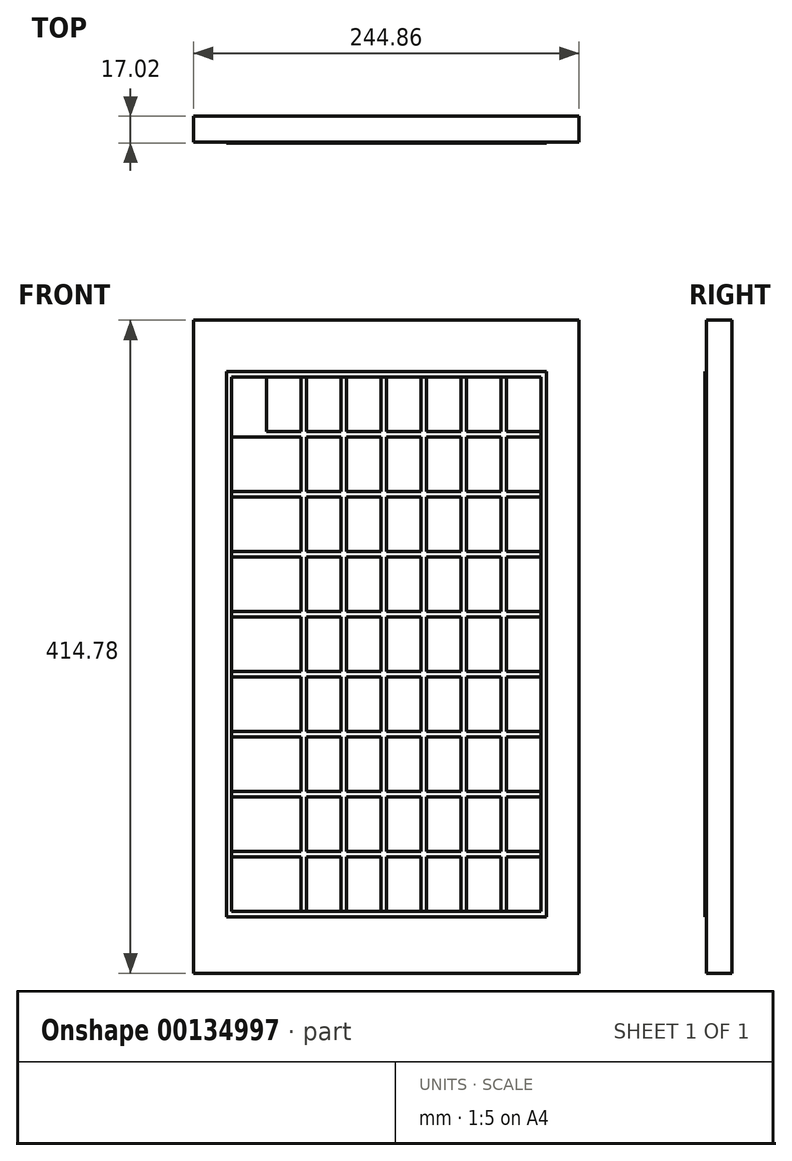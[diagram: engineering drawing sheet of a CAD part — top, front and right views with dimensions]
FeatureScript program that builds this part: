
annotation { "Feature Type Name" : "Feature", "Feature Type Description" : "" }
export const myFeature = defineFeature(function(context is Context, id is Id, definition is map)
    precondition{}
    {
        {
            var Q0;
            Q0=qCreatedBy(makeId("Front.planeOp"),FACE);
            var sketch = newSketch(context, id + "F0", { "sketchPlane" : qUnion([Q0])});
            skLineSegment(sketch, "E0.bottom", {"start": v(122.43, 207.4) * mm, "end": v(-122.43, 207.4) * mm});
            skLineSegment(sketch, "E0.top", {"start": v(122.43, -207.4) * mm, "end": v(-122.43, -207.4) * mm});
            skLineSegment(sketch, "E0.left", {"start": v(122.43, 207.4) * mm, "end": v(122.43, -207.4) * mm});
            skLineSegment(sketch, "E0.right", {"start": v(-122.43, 207.4) * mm, "end": v(-122.43, -207.4) * mm});
            skPoint(sketch, "E0.middle", {"position": v(0, 0) * mm});
            skSolve(sketch);
        }
        {
            var Q0;
            Q0=makeQuery(id+"F0.imprint","IMPRINT",FACE,{"disambiguationData":[TD([[makeQuery(id+"F0.imprint","IMPRINT",EDGE,{"derivedFrom":sQuery(id+"F0.wireOp",EDGE,"E0.bottom")}),1.0]])]});
            var sketch = newSketch(context, id + "F1", { "sketchPlane" : qUnion([Q0])});
            skLineSegment(sketch, "E1.bottom", {"start": v(98.22, 171.45) * mm, "end": v(-98.22, 171.45) * mm});
            skLineSegment(sketch, "E1.top", {"start": v(101.6, -171.45) * mm, "end": v(-101.6, -171.45) * mm});
            skLineSegment(sketch, "E1.left", {"start": v(101.6, 171.45) * mm, "end": v(101.6, -171.45) * mm});
            skLineSegment(sketch, "E1.right", {"start": v(-101.6, 171.45) * mm, "end": v(-101.6, -171.45) * mm});
            skPoint(sketch, "E1.middle", {"position": v(0, 0) * mm});
            skLineSegment(sketch, "E2.bottom", {"start": v(-98.22, 171.45) * mm, "end": v(-76.2, 171.45) * mm});
            skLineSegment(sketch, "E2.top", {"start": v(-98.22, 133.35) * mm, "end": v(-76.2, 133.35) * mm});
            skLineSegment(sketch, "E2.left", {"start": v(-101.6, 171.45) * mm, "end": v(-101.6, 133.35) * mm});
            skLineSegment(sketch, "E2.right", {"start": v(-76.2, 171.45) * mm, "end": v(-76.2, 133.35) * mm});
            skLineSegment(sketch, "E3.1.0.0", {"start": v(-50.8, 171.45) * mm, "end": v(-50.8, 133.35) * mm});
            skLineSegment(sketch, "E3.1.0.1", {"start": v(-76.2, 133.35) * mm, "end": v(-50.8, 133.35) * mm});
            skLineSegment(sketch, "E3.2.0.0", {"start": v(-25.4, 171.45) * mm, "end": v(-25.4, 133.35) * mm});
            skLineSegment(sketch, "E3.2.0.1", {"start": v(-50.8, 133.35) * mm, "end": v(-25.4, 133.35) * mm});
            skLineSegment(sketch, "E3.3.0.0", {"start": v(0, 171.45) * mm, "end": v(0, 133.35) * mm});
            skLineSegment(sketch, "E3.3.0.1", {"start": v(-25.4, 133.35) * mm, "end": v(0, 133.35) * mm});
            skLineSegment(sketch, "E3.4.0.0", {"start": v(25.4, 171.45) * mm, "end": v(25.4, 133.35) * mm});
            skLineSegment(sketch, "E3.4.0.1", {"start": v(0, 133.35) * mm, "end": v(25.4, 133.35) * mm});
            skLineSegment(sketch, "E3.5.0.0", {"start": v(50.8, 171.45) * mm, "end": v(50.8, 133.35) * mm});
            skLineSegment(sketch, "E3.5.0.1", {"start": v(25.4, 133.35) * mm, "end": v(50.8, 133.35) * mm});
            skLineSegment(sketch, "E3.6.0.0", {"start": v(76.2, 171.45) * mm, "end": v(76.2, 133.35) * mm});
            skLineSegment(sketch, "E3.6.0.1", {"start": v(50.8, 133.35) * mm, "end": v(76.2, 133.35) * mm});
            skLineSegment(sketch, "E3.7.0.0", {"start": v(101.6, 171.45) * mm, "end": v(101.6, 133.35) * mm});
            skLineSegment(sketch, "E3.7.0.1", {"start": v(76.2, 133.35) * mm, "end": v(98.22, 133.35) * mm});
            skLineSegment(sketch, "E3.direction1", {"start": v(-76.2, 133.35) * mm, "end": v(-50.8, 133.35) * mm, "construction": true});
            skLineSegment(sketch, "E4.0.1.0", {"start": v(-98.22, 95.25) * mm, "end": v(-76.2, 95.25) * mm});
            skLineSegment(sketch, "E4.0.1.1", {"start": v(-76.2, 133.35) * mm, "end": v(-76.2, 95.25) * mm});
            skLineSegment(sketch, "E4.0.2.0", {"start": v(-98.22, 57.15) * mm, "end": v(-76.2, 57.15) * mm});
            skLineSegment(sketch, "E4.0.2.1", {"start": v(-76.2, 95.25) * mm, "end": v(-76.2, 57.15) * mm});
            skLineSegment(sketch, "E4.0.3.0", {"start": v(-98.22, 19.05) * mm, "end": v(-76.2, 19.05) * mm});
            skLineSegment(sketch, "E4.0.3.1", {"start": v(-76.2, 57.15) * mm, "end": v(-76.2, 19.05) * mm});
            skLineSegment(sketch, "E4.0.4.0", {"start": v(-98.22, -19.05) * mm, "end": v(-76.2, -19.05) * mm});
            skLineSegment(sketch, "E4.0.4.1", {"start": v(-76.2, 19.05) * mm, "end": v(-76.2, -19.05) * mm});
            skLineSegment(sketch, "E4.0.5.0", {"start": v(-98.22, -57.15) * mm, "end": v(-76.2, -57.15) * mm});
            skLineSegment(sketch, "E4.0.5.1", {"start": v(-76.2, -19.05) * mm, "end": v(-76.2, -57.15) * mm});
            skLineSegment(sketch, "E4.0.6.0", {"start": v(-98.22, -95.25) * mm, "end": v(-76.2, -95.25) * mm});
            skLineSegment(sketch, "E4.0.6.1", {"start": v(-76.2, -57.15) * mm, "end": v(-76.2, -95.25) * mm});
            skLineSegment(sketch, "E4.0.7.0", {"start": v(-98.22, -133.35) * mm, "end": v(-76.2, -133.35) * mm});
            skLineSegment(sketch, "E4.0.7.1", {"start": v(-76.2, -95.25) * mm, "end": v(-76.2, -133.35) * mm});
            skLineSegment(sketch, "E4.0.8.0", {"start": v(-101.6, -171.45) * mm, "end": v(-76.2, -171.45) * mm});
            skLineSegment(sketch, "E4.0.8.1", {"start": v(-76.2, -133.35) * mm, "end": v(-76.2, -168.07) * mm});
            skLineSegment(sketch, "E4.1.1.0", {"start": v(-76.2, 95.25) * mm, "end": v(-50.8, 95.25) * mm});
            skLineSegment(sketch, "E4.1.1.1", {"start": v(-50.8, 133.35) * mm, "end": v(-50.8, 95.25) * mm});
            skLineSegment(sketch, "E4.1.2.0", {"start": v(-76.2, 57.15) * mm, "end": v(-50.8, 57.15) * mm});
            skLineSegment(sketch, "E4.1.2.1", {"start": v(-50.8, 95.25) * mm, "end": v(-50.8, 57.15) * mm});
            skLineSegment(sketch, "E4.1.3.0", {"start": v(-76.2, 19.05) * mm, "end": v(-50.8, 19.05) * mm});
            skLineSegment(sketch, "E4.1.3.1", {"start": v(-50.8, 57.15) * mm, "end": v(-50.8, 19.05) * mm});
            skLineSegment(sketch, "E4.1.4.0", {"start": v(-76.2, -19.05) * mm, "end": v(-50.8, -19.05) * mm});
            skLineSegment(sketch, "E4.1.4.1", {"start": v(-50.8, 19.05) * mm, "end": v(-50.8, -19.05) * mm});
            skLineSegment(sketch, "E4.1.5.0", {"start": v(-76.2, -57.15) * mm, "end": v(-50.8, -57.15) * mm});
            skLineSegment(sketch, "E4.1.5.1", {"start": v(-50.8, -19.05) * mm, "end": v(-50.8, -57.15) * mm});
            skLineSegment(sketch, "E4.1.6.0", {"start": v(-76.2, -95.25) * mm, "end": v(-50.8, -95.25) * mm});
            skLineSegment(sketch, "E4.1.6.1", {"start": v(-50.8, -57.15) * mm, "end": v(-50.8, -95.25) * mm});
            skLineSegment(sketch, "E4.1.7.0", {"start": v(-76.2, -133.35) * mm, "end": v(-50.8, -133.35) * mm});
            skLineSegment(sketch, "E4.1.7.1", {"start": v(-50.8, -95.25) * mm, "end": v(-50.8, -133.35) * mm});
            skLineSegment(sketch, "E4.1.8.0", {"start": v(-76.2, -171.45) * mm, "end": v(-50.8, -171.45) * mm});
            skLineSegment(sketch, "E4.1.8.1", {"start": v(-50.8, -133.35) * mm, "end": v(-50.8, -168.07) * mm});
            skLineSegment(sketch, "E4.2.1.0", {"start": v(-50.8, 95.25) * mm, "end": v(-25.4, 95.25) * mm});
            skLineSegment(sketch, "E4.2.1.1", {"start": v(-25.4, 133.35) * mm, "end": v(-25.4, 95.25) * mm});
            skLineSegment(sketch, "E4.2.2.0", {"start": v(-50.8, 57.15) * mm, "end": v(-25.4, 57.15) * mm});
            skLineSegment(sketch, "E4.2.2.1", {"start": v(-25.4, 95.25) * mm, "end": v(-25.4, 57.15) * mm});
            skLineSegment(sketch, "E4.2.3.0", {"start": v(-50.8, 19.05) * mm, "end": v(-25.4, 19.05) * mm});
            skLineSegment(sketch, "E4.2.3.1", {"start": v(-25.4, 57.15) * mm, "end": v(-25.4, 19.05) * mm});
            skLineSegment(sketch, "E4.2.4.0", {"start": v(-50.8, -19.05) * mm, "end": v(-25.4, -19.05) * mm});
            skLineSegment(sketch, "E4.2.4.1", {"start": v(-25.4, 19.05) * mm, "end": v(-25.4, -19.05) * mm});
            skLineSegment(sketch, "E4.2.5.0", {"start": v(-50.8, -57.15) * mm, "end": v(-25.4, -57.15) * mm});
            skLineSegment(sketch, "E4.2.5.1", {"start": v(-25.4, -19.05) * mm, "end": v(-25.4, -57.15) * mm});
            skLineSegment(sketch, "E4.2.6.0", {"start": v(-50.8, -95.25) * mm, "end": v(-25.4, -95.25) * mm});
            skLineSegment(sketch, "E4.2.6.1", {"start": v(-25.4, -57.15) * mm, "end": v(-25.4, -95.25) * mm});
            skLineSegment(sketch, "E4.2.7.0", {"start": v(-50.8, -133.35) * mm, "end": v(-25.4, -133.35) * mm});
            skLineSegment(sketch, "E4.2.7.1", {"start": v(-25.4, -95.25) * mm, "end": v(-25.4, -133.35) * mm});
            skLineSegment(sketch, "E4.2.8.0", {"start": v(-50.8, -171.45) * mm, "end": v(-25.4, -171.45) * mm});
            skLineSegment(sketch, "E4.2.8.1", {"start": v(-25.4, -133.35) * mm, "end": v(-25.4, -168.07) * mm});
            skLineSegment(sketch, "E4.3.1.0", {"start": v(-25.4, 95.25) * mm, "end": v(0, 95.25) * mm});
            skLineSegment(sketch, "E4.3.1.1", {"start": v(0, 133.35) * mm, "end": v(0, 95.25) * mm});
            skLineSegment(sketch, "E4.3.2.0", {"start": v(-25.4, 57.15) * mm, "end": v(0, 57.15) * mm});
            skLineSegment(sketch, "E4.3.2.1", {"start": v(0, 95.25) * mm, "end": v(0, 57.15) * mm});
            skLineSegment(sketch, "E4.3.3.0", {"start": v(-25.4, 19.05) * mm, "end": v(0, 19.05) * mm});
            skLineSegment(sketch, "E4.3.3.1", {"start": v(0, 57.15) * mm, "end": v(0, 19.05) * mm});
            skLineSegment(sketch, "E4.3.4.0", {"start": v(-25.4, -19.05) * mm, "end": v(0, -19.05) * mm});
            skLineSegment(sketch, "E4.3.4.1", {"start": v(0, 19.05) * mm, "end": v(0, -19.05) * mm});
            skLineSegment(sketch, "E4.3.5.0", {"start": v(-25.4, -57.15) * mm, "end": v(0, -57.15) * mm});
            skLineSegment(sketch, "E4.3.5.1", {"start": v(0, -19.05) * mm, "end": v(0, -57.15) * mm});
            skLineSegment(sketch, "E4.3.6.0", {"start": v(-25.4, -95.25) * mm, "end": v(0, -95.25) * mm});
            skLineSegment(sketch, "E4.3.6.1", {"start": v(0, -57.15) * mm, "end": v(0, -95.25) * mm});
            skLineSegment(sketch, "E4.3.7.0", {"start": v(-25.4, -133.35) * mm, "end": v(0, -133.35) * mm});
            skLineSegment(sketch, "E4.3.7.1", {"start": v(0, -95.25) * mm, "end": v(0, -133.35) * mm});
            skLineSegment(sketch, "E4.3.8.0", {"start": v(-25.4, -171.45) * mm, "end": v(0, -171.45) * mm});
            skLineSegment(sketch, "E4.3.8.1", {"start": v(0, -133.35) * mm, "end": v(0, -168.07) * mm});
            skLineSegment(sketch, "E4.4.1.0", {"start": v(0, 95.25) * mm, "end": v(25.4, 95.25) * mm});
            skLineSegment(sketch, "E4.4.1.1", {"start": v(25.4, 133.35) * mm, "end": v(25.4, 95.25) * mm});
            skLineSegment(sketch, "E4.4.2.0", {"start": v(0, 57.15) * mm, "end": v(25.4, 57.15) * mm});
            skLineSegment(sketch, "E4.4.2.1", {"start": v(25.4, 95.25) * mm, "end": v(25.4, 57.15) * mm});
            skLineSegment(sketch, "E4.4.3.0", {"start": v(0, 19.05) * mm, "end": v(25.4, 19.05) * mm});
            skLineSegment(sketch, "E4.4.3.1", {"start": v(25.4, 57.15) * mm, "end": v(25.4, 19.05) * mm});
            skLineSegment(sketch, "E4.4.4.0", {"start": v(0, -19.05) * mm, "end": v(25.4, -19.05) * mm});
            skLineSegment(sketch, "E4.4.4.1", {"start": v(25.4, 19.05) * mm, "end": v(25.4, -19.05) * mm});
            skLineSegment(sketch, "E4.4.5.0", {"start": v(0, -57.15) * mm, "end": v(25.4, -57.15) * mm});
            skLineSegment(sketch, "E4.4.5.1", {"start": v(25.4, -19.05) * mm, "end": v(25.4, -57.15) * mm});
            skLineSegment(sketch, "E4.4.6.0", {"start": v(0, -95.25) * mm, "end": v(25.4, -95.25) * mm});
            skLineSegment(sketch, "E4.4.6.1", {"start": v(25.4, -57.15) * mm, "end": v(25.4, -95.25) * mm});
            skLineSegment(sketch, "E4.4.7.0", {"start": v(0, -133.35) * mm, "end": v(25.4, -133.35) * mm});
            skLineSegment(sketch, "E4.4.7.1", {"start": v(25.4, -95.25) * mm, "end": v(25.4, -133.35) * mm});
            skLineSegment(sketch, "E4.4.8.0", {"start": v(0, -171.45) * mm, "end": v(25.4, -171.45) * mm});
            skLineSegment(sketch, "E4.4.8.1", {"start": v(25.4, -133.35) * mm, "end": v(25.4, -168.07) * mm});
            skLineSegment(sketch, "E4.5.1.0", {"start": v(25.4, 95.25) * mm, "end": v(50.8, 95.25) * mm});
            skLineSegment(sketch, "E4.5.1.1", {"start": v(50.8, 133.35) * mm, "end": v(50.8, 95.25) * mm});
            skLineSegment(sketch, "E4.5.2.0", {"start": v(25.4, 57.15) * mm, "end": v(50.8, 57.15) * mm});
            skLineSegment(sketch, "E4.5.2.1", {"start": v(50.8, 95.25) * mm, "end": v(50.8, 57.15) * mm});
            skLineSegment(sketch, "E4.5.3.0", {"start": v(25.4, 19.05) * mm, "end": v(50.8, 19.05) * mm});
            skLineSegment(sketch, "E4.5.3.1", {"start": v(50.8, 57.15) * mm, "end": v(50.8, 19.05) * mm});
            skLineSegment(sketch, "E4.5.4.0", {"start": v(25.4, -19.05) * mm, "end": v(50.8, -19.05) * mm});
            skLineSegment(sketch, "E4.5.4.1", {"start": v(50.8, 19.05) * mm, "end": v(50.8, -19.05) * mm});
            skLineSegment(sketch, "E4.5.5.0", {"start": v(25.4, -57.15) * mm, "end": v(50.8, -57.15) * mm});
            skLineSegment(sketch, "E4.5.5.1", {"start": v(50.8, -19.05) * mm, "end": v(50.8, -57.15) * mm});
            skLineSegment(sketch, "E4.5.6.0", {"start": v(25.4, -95.25) * mm, "end": v(50.8, -95.25) * mm});
            skLineSegment(sketch, "E4.5.6.1", {"start": v(50.8, -57.15) * mm, "end": v(50.8, -95.25) * mm});
            skLineSegment(sketch, "E4.5.7.0", {"start": v(25.4, -133.35) * mm, "end": v(50.8, -133.35) * mm});
            skLineSegment(sketch, "E4.5.7.1", {"start": v(50.8, -95.25) * mm, "end": v(50.8, -133.35) * mm});
            skLineSegment(sketch, "E4.5.8.0", {"start": v(25.4, -171.45) * mm, "end": v(50.8, -171.45) * mm});
            skLineSegment(sketch, "E4.5.8.1", {"start": v(50.8, -133.35) * mm, "end": v(50.8, -168.07) * mm});
            skLineSegment(sketch, "E4.6.1.0", {"start": v(50.8, 95.25) * mm, "end": v(76.2, 95.25) * mm});
            skLineSegment(sketch, "E4.6.1.1", {"start": v(76.2, 133.35) * mm, "end": v(76.2, 95.25) * mm});
            skLineSegment(sketch, "E4.6.2.0", {"start": v(50.8, 57.15) * mm, "end": v(76.2, 57.15) * mm});
            skLineSegment(sketch, "E4.6.2.1", {"start": v(76.2, 95.25) * mm, "end": v(76.2, 57.15) * mm});
            skLineSegment(sketch, "E4.6.3.0", {"start": v(50.8, 19.05) * mm, "end": v(76.2, 19.05) * mm});
            skLineSegment(sketch, "E4.6.3.1", {"start": v(76.2, 57.15) * mm, "end": v(76.2, 19.05) * mm});
            skLineSegment(sketch, "E4.6.4.0", {"start": v(50.8, -19.05) * mm, "end": v(76.2, -19.05) * mm});
            skLineSegment(sketch, "E4.6.4.1", {"start": v(76.2, 19.05) * mm, "end": v(76.2, -19.05) * mm});
            skLineSegment(sketch, "E4.6.5.0", {"start": v(50.8, -57.15) * mm, "end": v(76.2, -57.15) * mm});
            skLineSegment(sketch, "E4.6.5.1", {"start": v(76.2, -19.05) * mm, "end": v(76.2, -57.15) * mm});
            skLineSegment(sketch, "E4.6.6.0", {"start": v(50.8, -95.25) * mm, "end": v(76.2, -95.25) * mm});
            skLineSegment(sketch, "E4.6.6.1", {"start": v(76.2, -57.15) * mm, "end": v(76.2, -95.25) * mm});
            skLineSegment(sketch, "E4.6.7.0", {"start": v(50.8, -133.35) * mm, "end": v(76.2, -133.35) * mm});
            skLineSegment(sketch, "E4.6.7.1", {"start": v(76.2, -95.25) * mm, "end": v(76.2, -133.35) * mm});
            skLineSegment(sketch, "E4.6.8.0", {"start": v(50.8, -171.45) * mm, "end": v(76.2, -171.45) * mm});
            skLineSegment(sketch, "E4.6.8.1", {"start": v(76.2, -133.35) * mm, "end": v(76.2, -168.07) * mm});
            skLineSegment(sketch, "E4.7.1.0", {"start": v(76.2, 95.25) * mm, "end": v(98.22, 95.25) * mm});
            skLineSegment(sketch, "E4.7.1.1", {"start": v(101.6, 133.35) * mm, "end": v(101.6, 95.25) * mm});
            skLineSegment(sketch, "E4.7.2.0", {"start": v(76.2, 57.15) * mm, "end": v(98.22, 57.15) * mm});
            skLineSegment(sketch, "E4.7.2.1", {"start": v(101.6, 95.25) * mm, "end": v(101.6, 57.15) * mm});
            skLineSegment(sketch, "E4.7.3.0", {"start": v(76.2, 19.05) * mm, "end": v(98.22, 19.05) * mm});
            skLineSegment(sketch, "E4.7.3.1", {"start": v(101.6, 57.15) * mm, "end": v(101.6, 19.05) * mm});
            skLineSegment(sketch, "E4.7.4.0", {"start": v(76.2, -19.05) * mm, "end": v(98.22, -19.05) * mm});
            skLineSegment(sketch, "E4.7.4.1", {"start": v(101.6, 19.05) * mm, "end": v(101.6, -19.05) * mm});
            skLineSegment(sketch, "E4.7.5.0", {"start": v(76.2, -57.15) * mm, "end": v(98.22, -57.15) * mm});
            skLineSegment(sketch, "E4.7.5.1", {"start": v(101.6, -19.05) * mm, "end": v(101.6, -57.15) * mm});
            skLineSegment(sketch, "E4.7.6.0", {"start": v(76.2, -95.25) * mm, "end": v(98.22, -95.25) * mm});
            skLineSegment(sketch, "E4.7.6.1", {"start": v(101.6, -57.15) * mm, "end": v(101.6, -95.25) * mm});
            skLineSegment(sketch, "E4.7.7.0", {"start": v(76.2, -133.35) * mm, "end": v(98.22, -133.35) * mm});
            skLineSegment(sketch, "E4.7.7.1", {"start": v(101.6, -95.25) * mm, "end": v(101.6, -133.35) * mm});
            skLineSegment(sketch, "E4.7.8.0", {"start": v(76.2, -171.45) * mm, "end": v(101.6, -171.45) * mm});
            skLineSegment(sketch, "E4.7.8.1", {"start": v(101.6, -133.35) * mm, "end": v(101.6, -171.45) * mm});
            skLineSegment(sketch, "E4.direction1", {"start": v(-98.22, 133.35) * mm, "end": v(-76.2, 133.35) * mm, "construction": true});
            skLineSegment(sketch, "E4.direction2", {"start": v(-101.6, 133.35) * mm, "end": v(-101.6, 95.25) * mm, "construction": true});
            skLineSegment(sketch, "E5.0", {"start": v(98.22, 171.45) * mm, "end": v(98.22, -168.07) * mm});
            skLineSegment(sketch, "E6.0", {"start": v(-98.22, 171.45) * mm, "end": v(-98.22, -168.07) * mm});
            skLineSegment(sketch, "E7.1.0.0", {"start": v(72.82, 171.45) * mm, "end": v(72.82, -168.07) * mm});
            skLineSegment(sketch, "E7.2.0.0", {"start": v(47.42, 171.45) * mm, "end": v(47.42, -168.07) * mm});
            skLineSegment(sketch, "E7.3.0.0", {"start": v(22.02, 171.45) * mm, "end": v(22.02, -168.07) * mm});
            skLineSegment(sketch, "E7.4.0.0", {"start": v(-3.38, 171.45) * mm, "end": v(-3.38, -168.07) * mm});
            skLineSegment(sketch, "E7.5.0.0", {"start": v(-28.78, 171.45) * mm, "end": v(-28.78, -168.07) * mm});
            skLineSegment(sketch, "E7.6.0.0", {"start": v(-54.18, 171.45) * mm, "end": v(-54.18, -168.07) * mm});
            skLineSegment(sketch, "E7.7.0.0", {"start": v(-79.58, 171.45) * mm, "end": v(-79.58, -168.07) * mm});
            skLineSegment(sketch, "E7.direction1", {"start": v(98.22, -171.45) * mm, "end": v(72.82, -171.45) * mm, "construction": true});
            skLineSegment(sketch, "E8.0", {"start": v(98.22, -168.07) * mm, "end": v(-98.22, -168.07) * mm});
            skLineSegment(sketch, "E9.0.1.0", {"start": v(98.22, -129.97) * mm, "end": v(-98.22, -129.97) * mm});
            skLineSegment(sketch, "E9.0.2.0", {"start": v(98.22, -91.87) * mm, "end": v(-98.22, -91.87) * mm});
            skLineSegment(sketch, "E9.0.3.0", {"start": v(98.22, -53.77) * mm, "end": v(-98.22, -53.77) * mm});
            skLineSegment(sketch, "E9.0.4.0", {"start": v(98.22, -15.67) * mm, "end": v(-98.22, -15.67) * mm});
            skLineSegment(sketch, "E9.0.5.0", {"start": v(98.22, 22.43) * mm, "end": v(-98.22, 22.43) * mm});
            skLineSegment(sketch, "E9.0.6.0", {"start": v(98.22, 60.53) * mm, "end": v(-98.22, 60.53) * mm});
            skLineSegment(sketch, "E9.0.7.0", {"start": v(98.22, 98.63) * mm, "end": v(-98.22, 98.63) * mm});
            skLineSegment(sketch, "E9.0.8.0", {"start": v(98.22, 136.73) * mm, "end": v(-98.22, 136.73) * mm});
            skLineSegment(sketch, "E9.1.0.0", {"start": v(98.22, -168.07) * mm, "end": v(-76.2, -168.07) * mm});
            skLineSegment(sketch, "E9.1.1.0", {"start": v(98.22, -129.97) * mm, "end": v(-76.2, -129.97) * mm});
            skLineSegment(sketch, "E9.1.2.0", {"start": v(98.22, -91.87) * mm, "end": v(-76.2, -91.87) * mm});
            skLineSegment(sketch, "E9.1.3.0", {"start": v(98.22, -53.77) * mm, "end": v(-76.2, -53.77) * mm});
            skLineSegment(sketch, "E9.1.4.0", {"start": v(98.22, -15.67) * mm, "end": v(-76.2, -15.67) * mm});
            skLineSegment(sketch, "E9.1.5.0", {"start": v(98.22, 22.43) * mm, "end": v(-76.2, 22.43) * mm});
            skLineSegment(sketch, "E9.1.6.0", {"start": v(98.22, 60.53) * mm, "end": v(-76.2, 60.53) * mm});
            skLineSegment(sketch, "E9.1.7.0", {"start": v(98.22, 98.63) * mm, "end": v(-76.2, 98.63) * mm});
            skLineSegment(sketch, "E9.1.8.0", {"start": v(98.22, 136.73) * mm, "end": v(-76.2, 136.73) * mm});
            skLineSegment(sketch, "E9.2.0.0", {"start": v(98.22, -168.07) * mm, "end": v(-50.8, -168.07) * mm});
            skLineSegment(sketch, "E9.2.1.0", {"start": v(98.22, -129.97) * mm, "end": v(-50.8, -129.97) * mm});
            skLineSegment(sketch, "E9.2.2.0", {"start": v(98.22, -91.87) * mm, "end": v(-50.8, -91.87) * mm});
            skLineSegment(sketch, "E9.2.3.0", {"start": v(98.22, -53.77) * mm, "end": v(-50.8, -53.77) * mm});
            skLineSegment(sketch, "E9.2.4.0", {"start": v(98.22, -15.67) * mm, "end": v(-50.8, -15.67) * mm});
            skLineSegment(sketch, "E9.2.5.0", {"start": v(98.22, 22.43) * mm, "end": v(-50.8, 22.43) * mm});
            skLineSegment(sketch, "E9.2.6.0", {"start": v(98.22, 60.53) * mm, "end": v(-50.8, 60.53) * mm});
            skLineSegment(sketch, "E9.2.7.0", {"start": v(98.22, 98.63) * mm, "end": v(-50.8, 98.63) * mm});
            skLineSegment(sketch, "E9.2.8.0", {"start": v(98.22, 136.73) * mm, "end": v(-50.8, 136.73) * mm});
            skLineSegment(sketch, "E9.direction1", {"start": v(-98.22, -168.07) * mm, "end": v(-76.2, -168.07) * mm, "construction": true});
            skLineSegment(sketch, "E9.direction2", {"start": v(-101.6, -168.07) * mm, "end": v(-101.6, -129.97) * mm, "construction": true});
            skPoint(sketch, "E10.orphan", {"position": v(152.4, 136.73) * mm});
            skPoint(sketch, "E11.orphan", {"position": v(127, 136.73) * mm});
            skPoint(sketch, "E12.orphan", {"position": v(152.4, 98.63) * mm});
            skPoint(sketch, "E13.orphan", {"position": v(152.4, 60.53) * mm});
            skPoint(sketch, "E14.orphan", {"position": v(127, 98.63) * mm});
            skPoint(sketch, "E15.orphan", {"position": v(127, 60.53) * mm});
            skPoint(sketch, "E16.orphan", {"position": v(152.4, 22.43) * mm});
            skPoint(sketch, "E17.orphan", {"position": v(127, 22.43) * mm});
            skPoint(sketch, "E18.orphan", {"position": v(152.4, -15.67) * mm});
            skPoint(sketch, "E19.orphan", {"position": v(152.4, -53.77) * mm});
            skPoint(sketch, "E20.orphan", {"position": v(127, -15.67) * mm});
            skPoint(sketch, "E21.orphan", {"position": v(127, -53.77) * mm});
            skPoint(sketch, "E22.orphan", {"position": v(152.4, -91.87) * mm});
            skPoint(sketch, "E23.orphan", {"position": v(152.4, -129.97) * mm});
            skPoint(sketch, "E24.orphan", {"position": v(152.4, -168.07) * mm});
            skPoint(sketch, "E25.orphan", {"position": v(127, -168.07) * mm});
            skPoint(sketch, "E26.orphan", {"position": v(127, -129.97) * mm});
            skPoint(sketch, "E27.orphan", {"position": v(127, -91.87) * mm});
            skLineSegment(sketch, "E28", {"start": v(-101.6, 171.45) * mm, "end": v(-101.6, 174.83) * mm});
            skLineSegment(sketch, "E29", {"start": v(-101.6, 174.83) * mm, "end": v(98.22, 174.83) * mm});
            skLineSegment(sketch, "E30", {"start": v(98.22, 174.83) * mm, "end": v(101.6, 174.83) * mm});
            skLineSegment(sketch, "E31", {"start": v(101.6, 174.83) * mm, "end": v(101.6, 171.45) * mm});
            skPoint(sketch, "E32.orphan", {"position": v(-101.6, 136.73) * mm});
            skPoint(sketch, "E33.orphan", {"position": v(-101.6, 98.63) * mm});
            skPoint(sketch, "E34.orphan", {"position": v(-101.6, 60.53) * mm});
            skPoint(sketch, "E35.orphan", {"position": v(-101.6, 57.15) * mm});
            skPoint(sketch, "E36.orphan", {"position": v(-101.6, 22.43) * mm});
            skPoint(sketch, "E37.orphan", {"position": v(-101.6, 19.05) * mm});
            skPoint(sketch, "E38.orphan", {"position": v(-101.6, -15.67) * mm});
            skPoint(sketch, "E39.orphan", {"position": v(-101.6, -19.05) * mm});
            skPoint(sketch, "E40.orphan", {"position": v(-101.6, -53.77) * mm});
            skPoint(sketch, "E41.orphan", {"position": v(-101.6, -57.15) * mm});
            skPoint(sketch, "E42.orphan", {"position": v(-101.6, -91.87) * mm});
            skPoint(sketch, "E43.orphan", {"position": v(-101.6, -95.25) * mm});
            skPoint(sketch, "E44.orphan", {"position": v(-101.6, -133.35) * mm});
            skPoint(sketch, "E45.orphan", {"position": v(-98.22, -171.45) * mm});
            skPoint(sketch, "E46.orphan", {"position": v(-79.58, -171.45) * mm});
            skPoint(sketch, "E47.orphan", {"position": v(-54.18, -171.45) * mm});
            skPoint(sketch, "E48.orphan", {"position": v(-28.78, -171.45) * mm});
            skPoint(sketch, "E49.orphan", {"position": v(-3.38, -171.45) * mm});
            skPoint(sketch, "E50.orphan", {"position": v(22.02, -171.45) * mm});
            skPoint(sketch, "E51.orphan", {"position": v(47.42, -171.45) * mm});
            skPoint(sketch, "E52.orphan", {"position": v(101.6, -168.07) * mm});
            skPoint(sketch, "E53.orphan", {"position": v(101.6, -129.97) * mm});
            skPoint(sketch, "E54.orphan", {"position": v(101.6, -91.87) * mm});
            skPoint(sketch, "E55.orphan", {"position": v(101.6, -53.77) * mm});
            skPoint(sketch, "E56.orphan", {"position": v(101.6, -15.67) * mm});
            skPoint(sketch, "E57.orphan", {"position": v(101.6, 22.43) * mm});
            skPoint(sketch, "E58.orphan", {"position": v(101.6, 60.53) * mm});
            skPoint(sketch, "E59.orphan", {"position": v(101.6, 98.63) * mm});
            skPoint(sketch, "E60.orphan", {"position": v(101.6, 136.73) * mm});
            skSolve(sketch);
        }
        {
            var Q0;
            Q0=makeQuery(id+"F0.imprint","IMPRINT",FACE,{"disambiguationData":[TD([[makeQuery(id+"F0.imprint","IMPRINT",EDGE,{"derivedFrom":sQuery(id+"F0.wireOp",EDGE,"E0.bottom")}),1.0]])]});
            extrude(context, id + "F2", {"entities" : qUnion([Q0]), "depth" : 16.26 * mm});
        }
        {
            var Q0;
            {var subQ0=sQuery(id+"F1.wireOp",EDGE,"E3.6.0.0");var subQ1=sQuery(id+"F1.wireOp",EDGE,"E1.bottom");var subQ2=makeQuery(id+"F1.imprint","INTERSECT",VERTEX,{"derivedFrom":[subQ1,subQ0]});Q0=makeQuery(id+"F1.imprint","IMPRINT",FACE,{"disambiguationData":[TD([[makeQuery(id+"F1.imprint","IMPRINT",EDGE,{"disambiguationData":[TD([[subQ2,1.0]])],"derivedFrom":subQ1}),1.0]])]});}
            var Q1;
            {var subQ0=sQuery(id+"F1.wireOp",EDGE,"E3.7.0.1");var subQ5=sQuery(id+"F1.wireOp",EDGE,"E5.0");var subQ6=makeQuery(id+"F1.imprint","INTERSECT",VERTEX,{"derivedFrom":[subQ0,subQ5]});Q1=makeQuery(id+"F1.imprint","IMPRINT",FACE,{"disambiguationData":[TD([[makeQuery(id+"F1.imprint","IMPRINT",EDGE,{"disambiguationData":[TD([[subQ6,-1.0]])],"derivedFrom":subQ5}),-1.0]])]});}
            var Q2;
            {var subQ0=sQuery(id+"F1.wireOp",EDGE,"E4.7.1.0");var subQ5=sQuery(id+"F1.wireOp",EDGE,"E5.0");var subQ6=makeQuery(id+"F1.imprint","INTERSECT",VERTEX,{"derivedFrom":[subQ0,subQ5]});Q2=makeQuery(id+"F1.imprint","IMPRINT",FACE,{"disambiguationData":[TD([[makeQuery(id+"F1.imprint","IMPRINT",EDGE,{"disambiguationData":[TD([[subQ6,-1.0]])],"derivedFrom":subQ5}),-1.0]])]});}
            var Q3;
            {var subQ0=sQuery(id+"F1.wireOp",EDGE,"E4.7.2.0");var subQ5=sQuery(id+"F1.wireOp",EDGE,"E5.0");var subQ6=makeQuery(id+"F1.imprint","INTERSECT",VERTEX,{"derivedFrom":[subQ0,subQ5]});Q3=makeQuery(id+"F1.imprint","IMPRINT",FACE,{"disambiguationData":[TD([[makeQuery(id+"F1.imprint","IMPRINT",EDGE,{"disambiguationData":[TD([[subQ6,-1.0]])],"derivedFrom":subQ5}),-1.0]])]});}
            var Q4;
            {var subQ0=sQuery(id+"F1.wireOp",EDGE,"E4.7.3.0");var subQ5=sQuery(id+"F1.wireOp",EDGE,"E5.0");var subQ6=makeQuery(id+"F1.imprint","INTERSECT",VERTEX,{"derivedFrom":[subQ0,subQ5]});Q4=makeQuery(id+"F1.imprint","IMPRINT",FACE,{"disambiguationData":[TD([[makeQuery(id+"F1.imprint","IMPRINT",EDGE,{"disambiguationData":[TD([[subQ6,-1.0]])],"derivedFrom":subQ5}),-1.0]])]});}
            var Q5;
            {var subQ0=sQuery(id+"F1.wireOp",EDGE,"E4.7.4.0");var subQ5=sQuery(id+"F1.wireOp",EDGE,"E5.0");var subQ6=makeQuery(id+"F1.imprint","INTERSECT",VERTEX,{"derivedFrom":[subQ0,subQ5]});Q5=makeQuery(id+"F1.imprint","IMPRINT",FACE,{"disambiguationData":[TD([[makeQuery(id+"F1.imprint","IMPRINT",EDGE,{"disambiguationData":[TD([[subQ6,-1.0]])],"derivedFrom":subQ5}),-1.0]])]});}
            var Q6;
            {var subQ0=sQuery(id+"F1.wireOp",EDGE,"E4.7.5.0");var subQ5=sQuery(id+"F1.wireOp",EDGE,"E5.0");var subQ7=makeQuery(id+"F1.imprint","INTERSECT",VERTEX,{"derivedFrom":[subQ0,subQ5]});Q6=makeQuery(id+"F1.imprint","IMPRINT",FACE,{"disambiguationData":[TD([[makeQuery(id+"F1.imprint","IMPRINT",EDGE,{"disambiguationData":[TD([[subQ7,-1.0]])],"derivedFrom":subQ5}),-1.0]])]});}
            var Q7;
            {var subQ0=sQuery(id+"F1.wireOp",EDGE,"E4.7.6.0");var subQ5=sQuery(id+"F1.wireOp",EDGE,"E5.0");var subQ6=makeQuery(id+"F1.imprint","INTERSECT",VERTEX,{"derivedFrom":[subQ0,subQ5]});Q7=makeQuery(id+"F1.imprint","IMPRINT",FACE,{"disambiguationData":[TD([[makeQuery(id+"F1.imprint","IMPRINT",EDGE,{"disambiguationData":[TD([[subQ6,-1.0]])],"derivedFrom":subQ5}),-1.0]])]});}
            var Q8;
            {var subQ0=sQuery(id+"F1.wireOp",EDGE,"E4.7.7.0");var subQ5=sQuery(id+"F1.wireOp",EDGE,"E5.0");var subQ6=makeQuery(id+"F1.imprint","INTERSECT",VERTEX,{"derivedFrom":[subQ0,subQ5]});Q8=makeQuery(id+"F1.imprint","IMPRINT",FACE,{"disambiguationData":[TD([[makeQuery(id+"F1.imprint","IMPRINT",EDGE,{"disambiguationData":[TD([[subQ6,-1.0]])],"derivedFrom":subQ5}),-1.0]])]});}
            var Q9;
            {var subQ0=sQuery(id+"F1.wireOp",EDGE,"E4.6.7.0");var subQ5=sQuery(id+"F1.wireOp",EDGE,"E7.1.0.0");var subQ6=makeQuery(id+"F1.imprint","INTERSECT",VERTEX,{"derivedFrom":[subQ0,subQ5]});Q9=makeQuery(id+"F1.imprint","IMPRINT",FACE,{"disambiguationData":[TD([[makeQuery(id+"F1.imprint","IMPRINT",EDGE,{"disambiguationData":[TD([[subQ6,-1.0]])],"derivedFrom":subQ5}),-1.0]])]});}
            var Q10;
            {var subQ0=sQuery(id+"F1.wireOp",EDGE,"E4.6.6.0");var subQ5=sQuery(id+"F1.wireOp",EDGE,"E7.1.0.0");var subQ6=makeQuery(id+"F1.imprint","INTERSECT",VERTEX,{"derivedFrom":[subQ0,subQ5]});Q10=makeQuery(id+"F1.imprint","IMPRINT",FACE,{"disambiguationData":[TD([[makeQuery(id+"F1.imprint","IMPRINT",EDGE,{"disambiguationData":[TD([[subQ6,-1.0]])],"derivedFrom":subQ5}),-1.0]])]});}
            var Q11;
            {var subQ0=sQuery(id+"F1.wireOp",EDGE,"E4.6.5.0");var subQ5=sQuery(id+"F1.wireOp",EDGE,"E7.1.0.0");var subQ6=makeQuery(id+"F1.imprint","INTERSECT",VERTEX,{"derivedFrom":[subQ0,subQ5]});Q11=makeQuery(id+"F1.imprint","IMPRINT",FACE,{"disambiguationData":[TD([[makeQuery(id+"F1.imprint","IMPRINT",EDGE,{"disambiguationData":[TD([[subQ6,-1.0]])],"derivedFrom":subQ5}),-1.0]])]});}
            var Q12;
            {var subQ0=sQuery(id+"F1.wireOp",EDGE,"E4.6.4.0");var subQ5=sQuery(id+"F1.wireOp",EDGE,"E7.1.0.0");var subQ6=makeQuery(id+"F1.imprint","INTERSECT",VERTEX,{"derivedFrom":[subQ0,subQ5]});Q12=makeQuery(id+"F1.imprint","IMPRINT",FACE,{"disambiguationData":[TD([[makeQuery(id+"F1.imprint","IMPRINT",EDGE,{"disambiguationData":[TD([[subQ6,-1.0]])],"derivedFrom":subQ5}),-1.0]])]});}
            var Q13;
            {var subQ0=sQuery(id+"F1.wireOp",EDGE,"E4.6.3.0");var subQ5=sQuery(id+"F1.wireOp",EDGE,"E7.1.0.0");var subQ6=makeQuery(id+"F1.imprint","INTERSECT",VERTEX,{"derivedFrom":[subQ0,subQ5]});Q13=makeQuery(id+"F1.imprint","IMPRINT",FACE,{"disambiguationData":[TD([[makeQuery(id+"F1.imprint","IMPRINT",EDGE,{"disambiguationData":[TD([[subQ6,-1.0]])],"derivedFrom":subQ5}),-1.0]])]});}
            var Q14;
            {var subQ0=sQuery(id+"F1.wireOp",EDGE,"E4.6.2.0");var subQ5=sQuery(id+"F1.wireOp",EDGE,"E7.1.0.0");var subQ6=makeQuery(id+"F1.imprint","INTERSECT",VERTEX,{"derivedFrom":[subQ0,subQ5]});Q14=makeQuery(id+"F1.imprint","IMPRINT",FACE,{"disambiguationData":[TD([[makeQuery(id+"F1.imprint","IMPRINT",EDGE,{"disambiguationData":[TD([[subQ6,-1.0]])],"derivedFrom":subQ5}),-1.0]])]});}
            var Q15;
            {var subQ0=sQuery(id+"F1.wireOp",EDGE,"E4.6.1.0");var subQ5=sQuery(id+"F1.wireOp",EDGE,"E7.1.0.0");var subQ6=makeQuery(id+"F1.imprint","INTERSECT",VERTEX,{"derivedFrom":[subQ0,subQ5]});Q15=makeQuery(id+"F1.imprint","IMPRINT",FACE,{"disambiguationData":[TD([[makeQuery(id+"F1.imprint","IMPRINT",EDGE,{"disambiguationData":[TD([[subQ6,-1.0]])],"derivedFrom":subQ5}),-1.0]])]});}
            var Q16;
            {var subQ0=sQuery(id+"F1.wireOp",EDGE,"E3.6.0.1");var subQ5=sQuery(id+"F1.wireOp",EDGE,"E7.1.0.0");var subQ6=makeQuery(id+"F1.imprint","INTERSECT",VERTEX,{"derivedFrom":[subQ0,subQ5]});Q16=makeQuery(id+"F1.imprint","IMPRINT",FACE,{"disambiguationData":[TD([[makeQuery(id+"F1.imprint","IMPRINT",EDGE,{"disambiguationData":[TD([[subQ6,-1.0]])],"derivedFrom":subQ5}),-1.0]])]});}
            var Q17;
            {var subQ0=sQuery(id+"F1.wireOp",EDGE,"E3.5.0.0");var subQ1=sQuery(id+"F1.wireOp",EDGE,"E1.bottom");var subQ2=makeQuery(id+"F1.imprint","INTERSECT",VERTEX,{"derivedFrom":[subQ1,subQ0]});Q17=makeQuery(id+"F1.imprint","IMPRINT",FACE,{"disambiguationData":[TD([[makeQuery(id+"F1.imprint","IMPRINT",EDGE,{"disambiguationData":[TD([[subQ2,1.0]])],"derivedFrom":subQ1}),1.0]])]});}
            var Q18;
            {var subQ0=sQuery(id+"F1.wireOp",EDGE,"E3.4.0.0");var subQ1=sQuery(id+"F1.wireOp",EDGE,"E1.bottom");var subQ2=makeQuery(id+"F1.imprint","INTERSECT",VERTEX,{"derivedFrom":[subQ1,subQ0]});Q18=makeQuery(id+"F1.imprint","IMPRINT",FACE,{"disambiguationData":[TD([[makeQuery(id+"F1.imprint","IMPRINT",EDGE,{"disambiguationData":[TD([[subQ2,1.0]])],"derivedFrom":subQ1}),1.0]])]});}
            var Q19;
            {var subQ0=sQuery(id+"F1.wireOp",EDGE,"E3.5.0.1");var subQ5=sQuery(id+"F1.wireOp",EDGE,"E7.2.0.0");var subQ6=makeQuery(id+"F1.imprint","INTERSECT",VERTEX,{"derivedFrom":[subQ0,subQ5]});Q19=makeQuery(id+"F1.imprint","IMPRINT",FACE,{"disambiguationData":[TD([[makeQuery(id+"F1.imprint","IMPRINT",EDGE,{"disambiguationData":[TD([[subQ6,-1.0]])],"derivedFrom":subQ5}),-1.0]])]});}
            var Q20;
            {var subQ0=sQuery(id+"F1.wireOp",EDGE,"E3.3.0.0");var subQ1=sQuery(id+"F1.wireOp",EDGE,"E1.bottom");var subQ2=makeQuery(id+"F1.imprint","INTERSECT",VERTEX,{"derivedFrom":[subQ1,subQ0]});Q20=makeQuery(id+"F1.imprint","IMPRINT",FACE,{"disambiguationData":[TD([[makeQuery(id+"F1.imprint","IMPRINT",EDGE,{"disambiguationData":[TD([[subQ2,1.0]])],"derivedFrom":subQ1}),1.0]])]});}
            var Q21;
            {var subQ0=sQuery(id+"F1.wireOp",EDGE,"E3.2.0.0");var subQ1=sQuery(id+"F1.wireOp",EDGE,"E1.bottom");var subQ2=makeQuery(id+"F1.imprint","INTERSECT",VERTEX,{"derivedFrom":[subQ1,subQ0]});Q21=makeQuery(id+"F1.imprint","IMPRINT",FACE,{"disambiguationData":[TD([[makeQuery(id+"F1.imprint","IMPRINT",EDGE,{"disambiguationData":[TD([[subQ2,1.0]])],"derivedFrom":subQ1}),1.0]])]});}
            var Q22;
            {var subQ0=sQuery(id+"F1.wireOp",EDGE,"E3.4.0.1");var subQ5=sQuery(id+"F1.wireOp",EDGE,"E7.3.0.0");var subQ6=makeQuery(id+"F1.imprint","INTERSECT",VERTEX,{"derivedFrom":[subQ0,subQ5]});Q22=makeQuery(id+"F1.imprint","IMPRINT",FACE,{"disambiguationData":[TD([[makeQuery(id+"F1.imprint","IMPRINT",EDGE,{"disambiguationData":[TD([[subQ6,-1.0]])],"derivedFrom":subQ5}),-1.0]])]});}
            var Q23;
            {var subQ0=sQuery(id+"F1.wireOp",EDGE,"E3.3.0.1");var subQ5=sQuery(id+"F1.wireOp",EDGE,"E7.4.0.0");var subQ6=makeQuery(id+"F1.imprint","INTERSECT",VERTEX,{"derivedFrom":[subQ0,subQ5]});Q23=makeQuery(id+"F1.imprint","IMPRINT",FACE,{"disambiguationData":[TD([[makeQuery(id+"F1.imprint","IMPRINT",EDGE,{"disambiguationData":[TD([[subQ6,-1.0]])],"derivedFrom":subQ5}),-1.0]])]});}
            var Q24;
            {var subQ0=sQuery(id+"F1.wireOp",EDGE,"E3.1.0.0");var subQ1=sQuery(id+"F1.wireOp",EDGE,"E1.bottom");var subQ2=makeQuery(id+"F1.imprint","INTERSECT",VERTEX,{"derivedFrom":[subQ1,subQ0]});Q24=makeQuery(id+"F1.imprint","IMPRINT",FACE,{"disambiguationData":[TD([[makeQuery(id+"F1.imprint","IMPRINT",EDGE,{"disambiguationData":[TD([[subQ2,1.0]])],"derivedFrom":subQ1}),1.0]])]});}
            var Q25;
            {var subQ0=sQuery(id+"F1.wireOp",EDGE,"E3.2.0.1");var subQ5=sQuery(id+"F1.wireOp",EDGE,"E7.5.0.0");var subQ7=makeQuery(id+"F1.imprint","INTERSECT",VERTEX,{"derivedFrom":[subQ0,subQ5]});Q25=makeQuery(id+"F1.imprint","IMPRINT",FACE,{"disambiguationData":[TD([[makeQuery(id+"F1.imprint","IMPRINT",EDGE,{"disambiguationData":[TD([[subQ7,-1.0]])],"derivedFrom":subQ5}),-1.0]])]});}
            var Q26;
            {var subQ1=sQuery(id+"F1.wireOp",EDGE,"E1.bottom");var subQ3=sQuery(id+"F1.wireOp",EDGE,"E7.6.0.0");var subQ4=makeQuery(id+"F1.imprint","INTERSECT",VERTEX,{"derivedFrom":[subQ1,subQ3]});Q26=makeQuery(id+"F1.imprint","IMPRINT",FACE,{"disambiguationData":[TD([[makeQuery(id+"F1.imprint","IMPRINT",EDGE,{"disambiguationData":[TD([[subQ4,-1.0]])],"derivedFrom":subQ3}),-1.0]])]});}
            var Q27;
            {var subQ0=sQuery(id+"F1.wireOp",EDGE,"E3.1.0.1");var subQ5=sQuery(id+"F1.wireOp",EDGE,"E7.6.0.0");var subQ7=makeQuery(id+"F1.imprint","INTERSECT",VERTEX,{"derivedFrom":[subQ0,subQ5]});Q27=makeQuery(id+"F1.imprint","IMPRINT",FACE,{"disambiguationData":[TD([[makeQuery(id+"F1.imprint","IMPRINT",EDGE,{"disambiguationData":[TD([[subQ7,-1.0]])],"derivedFrom":subQ5}),-1.0]])]});}
            var Q28;
            {var subQ0=sQuery(id+"F1.wireOp",EDGE,"E6.0");var subQ1=sQuery(id+"F1.wireOp",EDGE,"E2.bottom");var subQ2=makeQuery(id+"F1.imprint","INTERSECT",VERTEX,{"derivedFrom":[subQ1,subQ0]});Q28=makeQuery(id+"F1.imprint","IMPRINT",FACE,{"disambiguationData":[TD([[makeQuery(id+"F1.imprint","IMPRINT",EDGE,{"disambiguationData":[TD([[subQ2,-1.0]])],"derivedFrom":subQ1}),-1.0]])]});}
            var Q29;
            {var subQ0=sQuery(id+"F1.wireOp",EDGE,"E6.0");var subQ1=sQuery(id+"F1.wireOp",EDGE,"E2.top");var subQ2=makeQuery(id+"F1.imprint","INTERSECT",VERTEX,{"derivedFrom":[subQ1,subQ0]});Q29=makeQuery(id+"F1.imprint","IMPRINT",FACE,{"disambiguationData":[TD([[makeQuery(id+"F1.imprint","IMPRINT",EDGE,{"disambiguationData":[TD([[subQ2,-1.0]])],"derivedFrom":subQ1}),-1.0]])]});}
            var Q30;
            {var subQ0=sQuery(id+"F1.wireOp",EDGE,"E4.5.1.0");var subQ5=sQuery(id+"F1.wireOp",EDGE,"E7.2.0.0");var subQ6=makeQuery(id+"F1.imprint","INTERSECT",VERTEX,{"derivedFrom":[subQ0,subQ5]});Q30=makeQuery(id+"F1.imprint","IMPRINT",FACE,{"disambiguationData":[TD([[makeQuery(id+"F1.imprint","IMPRINT",EDGE,{"disambiguationData":[TD([[subQ6,-1.0]])],"derivedFrom":subQ5}),-1.0]])]});}
            var Q31;
            {var subQ0=sQuery(id+"F1.wireOp",EDGE,"E4.4.1.0");var subQ5=sQuery(id+"F1.wireOp",EDGE,"E7.3.0.0");var subQ6=makeQuery(id+"F1.imprint","INTERSECT",VERTEX,{"derivedFrom":[subQ0,subQ5]});Q31=makeQuery(id+"F1.imprint","IMPRINT",FACE,{"disambiguationData":[TD([[makeQuery(id+"F1.imprint","IMPRINT",EDGE,{"disambiguationData":[TD([[subQ6,-1.0]])],"derivedFrom":subQ5}),-1.0]])]});}
            var Q32;
            {var subQ0=sQuery(id+"F1.wireOp",EDGE,"E4.3.1.0");var subQ5=sQuery(id+"F1.wireOp",EDGE,"E7.4.0.0");var subQ6=makeQuery(id+"F1.imprint","INTERSECT",VERTEX,{"derivedFrom":[subQ0,subQ5]});Q32=makeQuery(id+"F1.imprint","IMPRINT",FACE,{"disambiguationData":[TD([[makeQuery(id+"F1.imprint","IMPRINT",EDGE,{"disambiguationData":[TD([[subQ6,-1.0]])],"derivedFrom":subQ5}),-1.0]])]});}
            var Q33;
            {var subQ0=sQuery(id+"F1.wireOp",EDGE,"E4.2.1.0");var subQ5=sQuery(id+"F1.wireOp",EDGE,"E7.5.0.0");var subQ6=makeQuery(id+"F1.imprint","INTERSECT",VERTEX,{"derivedFrom":[subQ0,subQ5]});Q33=makeQuery(id+"F1.imprint","IMPRINT",FACE,{"disambiguationData":[TD([[makeQuery(id+"F1.imprint","IMPRINT",EDGE,{"disambiguationData":[TD([[subQ6,-1.0]])],"derivedFrom":subQ5}),-1.0]])]});}
            var Q34;
            {var subQ0=sQuery(id+"F1.wireOp",EDGE,"E4.1.1.0");var subQ5=sQuery(id+"F1.wireOp",EDGE,"E7.6.0.0");var subQ7=makeQuery(id+"F1.imprint","INTERSECT",VERTEX,{"derivedFrom":[subQ0,subQ5]});Q34=makeQuery(id+"F1.imprint","IMPRINT",FACE,{"disambiguationData":[TD([[makeQuery(id+"F1.imprint","IMPRINT",EDGE,{"disambiguationData":[TD([[subQ7,-1.0]])],"derivedFrom":subQ5}),-1.0]])]});}
            var Q35;
            {var subQ0=sQuery(id+"F1.wireOp",EDGE,"E6.0");var subQ1=sQuery(id+"F1.wireOp",EDGE,"E4.0.1.0");var subQ2=makeQuery(id+"F1.imprint","INTERSECT",VERTEX,{"derivedFrom":[subQ1,subQ0]});Q35=makeQuery(id+"F1.imprint","IMPRINT",FACE,{"disambiguationData":[TD([[makeQuery(id+"F1.imprint","IMPRINT",EDGE,{"disambiguationData":[TD([[subQ2,-1.0]])],"derivedFrom":subQ1}),-1.0]])]});}
            var Q36;
            {var subQ0=sQuery(id+"F1.wireOp",EDGE,"E4.5.2.0");var subQ5=sQuery(id+"F1.wireOp",EDGE,"E7.2.0.0");var subQ6=makeQuery(id+"F1.imprint","INTERSECT",VERTEX,{"derivedFrom":[subQ0,subQ5]});Q36=makeQuery(id+"F1.imprint","IMPRINT",FACE,{"disambiguationData":[TD([[makeQuery(id+"F1.imprint","IMPRINT",EDGE,{"disambiguationData":[TD([[subQ6,-1.0]])],"derivedFrom":subQ5}),-1.0]])]});}
            var Q37;
            {var subQ0=sQuery(id+"F1.wireOp",EDGE,"E4.4.2.0");var subQ5=sQuery(id+"F1.wireOp",EDGE,"E7.3.0.0");var subQ6=makeQuery(id+"F1.imprint","INTERSECT",VERTEX,{"derivedFrom":[subQ0,subQ5]});Q37=makeQuery(id+"F1.imprint","IMPRINT",FACE,{"disambiguationData":[TD([[makeQuery(id+"F1.imprint","IMPRINT",EDGE,{"disambiguationData":[TD([[subQ6,-1.0]])],"derivedFrom":subQ5}),-1.0]])]});}
            var Q38;
            {var subQ0=sQuery(id+"F1.wireOp",EDGE,"E4.3.2.0");var subQ5=sQuery(id+"F1.wireOp",EDGE,"E7.4.0.0");var subQ6=makeQuery(id+"F1.imprint","INTERSECT",VERTEX,{"derivedFrom":[subQ0,subQ5]});Q38=makeQuery(id+"F1.imprint","IMPRINT",FACE,{"disambiguationData":[TD([[makeQuery(id+"F1.imprint","IMPRINT",EDGE,{"disambiguationData":[TD([[subQ6,-1.0]])],"derivedFrom":subQ5}),-1.0]])]});}
            var Q39;
            {var subQ0=sQuery(id+"F1.wireOp",EDGE,"E4.2.2.0");var subQ5=sQuery(id+"F1.wireOp",EDGE,"E7.5.0.0");var subQ6=makeQuery(id+"F1.imprint","INTERSECT",VERTEX,{"derivedFrom":[subQ0,subQ5]});Q39=makeQuery(id+"F1.imprint","IMPRINT",FACE,{"disambiguationData":[TD([[makeQuery(id+"F1.imprint","IMPRINT",EDGE,{"disambiguationData":[TD([[subQ6,-1.0]])],"derivedFrom":subQ5}),-1.0]])]});}
            var Q40;
            {var subQ0=sQuery(id+"F1.wireOp",EDGE,"E4.1.2.0");var subQ5=sQuery(id+"F1.wireOp",EDGE,"E7.6.0.0");var subQ6=makeQuery(id+"F1.imprint","INTERSECT",VERTEX,{"derivedFrom":[subQ0,subQ5]});Q40=makeQuery(id+"F1.imprint","IMPRINT",FACE,{"disambiguationData":[TD([[makeQuery(id+"F1.imprint","IMPRINT",EDGE,{"disambiguationData":[TD([[subQ6,-1.0]])],"derivedFrom":subQ5}),-1.0]])]});}
            var Q41;
            {var subQ0=sQuery(id+"F1.wireOp",EDGE,"E6.0");var subQ1=sQuery(id+"F1.wireOp",EDGE,"E4.0.2.0");var subQ2=makeQuery(id+"F1.imprint","INTERSECT",VERTEX,{"derivedFrom":[subQ1,subQ0]});Q41=makeQuery(id+"F1.imprint","IMPRINT",FACE,{"disambiguationData":[TD([[makeQuery(id+"F1.imprint","IMPRINT",EDGE,{"disambiguationData":[TD([[subQ2,-1.0]])],"derivedFrom":subQ1}),-1.0]])]});}
            var Q42;
            {var subQ0=sQuery(id+"F1.wireOp",EDGE,"E4.5.3.0");var subQ5=sQuery(id+"F1.wireOp",EDGE,"E7.2.0.0");var subQ6=makeQuery(id+"F1.imprint","INTERSECT",VERTEX,{"derivedFrom":[subQ0,subQ5]});Q42=makeQuery(id+"F1.imprint","IMPRINT",FACE,{"disambiguationData":[TD([[makeQuery(id+"F1.imprint","IMPRINT",EDGE,{"disambiguationData":[TD([[subQ6,-1.0]])],"derivedFrom":subQ5}),-1.0]])]});}
            var Q43;
            {var subQ0=sQuery(id+"F1.wireOp",EDGE,"E4.4.3.0");var subQ5=sQuery(id+"F1.wireOp",EDGE,"E7.3.0.0");var subQ7=makeQuery(id+"F1.imprint","INTERSECT",VERTEX,{"derivedFrom":[subQ0,subQ5]});Q43=makeQuery(id+"F1.imprint","IMPRINT",FACE,{"disambiguationData":[TD([[makeQuery(id+"F1.imprint","IMPRINT",EDGE,{"disambiguationData":[TD([[subQ7,-1.0]])],"derivedFrom":subQ5}),-1.0]])]});}
            var Q44;
            {var subQ0=sQuery(id+"F1.wireOp",EDGE,"E4.3.3.0");var subQ5=sQuery(id+"F1.wireOp",EDGE,"E7.4.0.0");var subQ6=makeQuery(id+"F1.imprint","INTERSECT",VERTEX,{"derivedFrom":[subQ0,subQ5]});Q44=makeQuery(id+"F1.imprint","IMPRINT",FACE,{"disambiguationData":[TD([[makeQuery(id+"F1.imprint","IMPRINT",EDGE,{"disambiguationData":[TD([[subQ6,-1.0]])],"derivedFrom":subQ5}),-1.0]])]});}
            var Q45;
            {var subQ1=sQuery(id+"F1.wireOp",EDGE,"E4.2.3.0");var subQ3=sQuery(id+"F1.wireOp",EDGE,"E7.5.0.0");var subQ4=makeQuery(id+"F1.imprint","INTERSECT",VERTEX,{"derivedFrom":[subQ1,subQ3]});Q45=makeQuery(id+"F1.imprint","IMPRINT",FACE,{"disambiguationData":[TD([[makeQuery(id+"F1.imprint","IMPRINT",EDGE,{"disambiguationData":[TD([[subQ4,-1.0]])],"derivedFrom":subQ3}),-1.0]])]});}
            var Q46;
            {var subQ0=sQuery(id+"F1.wireOp",EDGE,"E4.1.3.0");var subQ5=sQuery(id+"F1.wireOp",EDGE,"E7.6.0.0");var subQ6=makeQuery(id+"F1.imprint","INTERSECT",VERTEX,{"derivedFrom":[subQ0,subQ5]});Q46=makeQuery(id+"F1.imprint","IMPRINT",FACE,{"disambiguationData":[TD([[makeQuery(id+"F1.imprint","IMPRINT",EDGE,{"disambiguationData":[TD([[subQ6,-1.0]])],"derivedFrom":subQ5}),-1.0]])]});}
            var Q47;
            {var subQ0=sQuery(id+"F1.wireOp",EDGE,"E6.0");var subQ1=sQuery(id+"F1.wireOp",EDGE,"E4.0.3.0");var subQ2=makeQuery(id+"F1.imprint","INTERSECT",VERTEX,{"derivedFrom":[subQ1,subQ0]});Q47=makeQuery(id+"F1.imprint","IMPRINT",FACE,{"disambiguationData":[TD([[makeQuery(id+"F1.imprint","IMPRINT",EDGE,{"disambiguationData":[TD([[subQ2,-1.0]])],"derivedFrom":subQ1}),-1.0]])]});}
            var Q48;
            {var subQ0=sQuery(id+"F1.wireOp",EDGE,"E4.5.4.0");var subQ5=sQuery(id+"F1.wireOp",EDGE,"E7.2.0.0");var subQ6=makeQuery(id+"F1.imprint","INTERSECT",VERTEX,{"derivedFrom":[subQ0,subQ5]});Q48=makeQuery(id+"F1.imprint","IMPRINT",FACE,{"disambiguationData":[TD([[makeQuery(id+"F1.imprint","IMPRINT",EDGE,{"disambiguationData":[TD([[subQ6,-1.0]])],"derivedFrom":subQ5}),-1.0]])]});}
            var Q49;
            {var subQ0=sQuery(id+"F1.wireOp",EDGE,"E4.4.4.0");var subQ5=sQuery(id+"F1.wireOp",EDGE,"E7.3.0.0");var subQ6=makeQuery(id+"F1.imprint","INTERSECT",VERTEX,{"derivedFrom":[subQ0,subQ5]});Q49=makeQuery(id+"F1.imprint","IMPRINT",FACE,{"disambiguationData":[TD([[makeQuery(id+"F1.imprint","IMPRINT",EDGE,{"disambiguationData":[TD([[subQ6,-1.0]])],"derivedFrom":subQ5}),-1.0]])]});}
            var Q50;
            {var subQ0=sQuery(id+"F1.wireOp",EDGE,"E4.3.4.0");var subQ5=sQuery(id+"F1.wireOp",EDGE,"E7.4.0.0");var subQ7=makeQuery(id+"F1.imprint","INTERSECT",VERTEX,{"derivedFrom":[subQ0,subQ5]});Q50=makeQuery(id+"F1.imprint","IMPRINT",FACE,{"disambiguationData":[TD([[makeQuery(id+"F1.imprint","IMPRINT",EDGE,{"disambiguationData":[TD([[subQ7,-1.0]])],"derivedFrom":subQ5}),-1.0]])]});}
            var Q51;
            {var subQ0=sQuery(id+"F1.wireOp",EDGE,"E4.2.4.0");var subQ5=sQuery(id+"F1.wireOp",EDGE,"E7.5.0.0");var subQ7=makeQuery(id+"F1.imprint","INTERSECT",VERTEX,{"derivedFrom":[subQ0,subQ5]});Q51=makeQuery(id+"F1.imprint","IMPRINT",FACE,{"disambiguationData":[TD([[makeQuery(id+"F1.imprint","IMPRINT",EDGE,{"disambiguationData":[TD([[subQ7,-1.0]])],"derivedFrom":subQ5}),-1.0]])]});}
            var Q52;
            {var subQ0=sQuery(id+"F1.wireOp",EDGE,"E4.1.4.0");var subQ5=sQuery(id+"F1.wireOp",EDGE,"E7.6.0.0");var subQ6=makeQuery(id+"F1.imprint","INTERSECT",VERTEX,{"derivedFrom":[subQ0,subQ5]});Q52=makeQuery(id+"F1.imprint","IMPRINT",FACE,{"disambiguationData":[TD([[makeQuery(id+"F1.imprint","IMPRINT",EDGE,{"disambiguationData":[TD([[subQ6,-1.0]])],"derivedFrom":subQ5}),-1.0]])]});}
            var Q53;
            {var subQ0=sQuery(id+"F1.wireOp",EDGE,"E6.0");var subQ1=sQuery(id+"F1.wireOp",EDGE,"E4.0.4.0");var subQ2=makeQuery(id+"F1.imprint","INTERSECT",VERTEX,{"derivedFrom":[subQ1,subQ0]});Q53=makeQuery(id+"F1.imprint","IMPRINT",FACE,{"disambiguationData":[TD([[makeQuery(id+"F1.imprint","IMPRINT",EDGE,{"disambiguationData":[TD([[subQ2,-1.0]])],"derivedFrom":subQ1}),-1.0]])]});}
            var Q54;
            {var subQ0=sQuery(id+"F1.wireOp",EDGE,"E4.5.5.0");var subQ5=sQuery(id+"F1.wireOp",EDGE,"E7.2.0.0");var subQ6=makeQuery(id+"F1.imprint","INTERSECT",VERTEX,{"derivedFrom":[subQ0,subQ5]});Q54=makeQuery(id+"F1.imprint","IMPRINT",FACE,{"disambiguationData":[TD([[makeQuery(id+"F1.imprint","IMPRINT",EDGE,{"disambiguationData":[TD([[subQ6,-1.0]])],"derivedFrom":subQ5}),-1.0]])]});}
            var Q55;
            {var subQ0=sQuery(id+"F1.wireOp",EDGE,"E4.4.5.0");var subQ5=sQuery(id+"F1.wireOp",EDGE,"E7.3.0.0");var subQ6=makeQuery(id+"F1.imprint","INTERSECT",VERTEX,{"derivedFrom":[subQ0,subQ5]});Q55=makeQuery(id+"F1.imprint","IMPRINT",FACE,{"disambiguationData":[TD([[makeQuery(id+"F1.imprint","IMPRINT",EDGE,{"disambiguationData":[TD([[subQ6,-1.0]])],"derivedFrom":subQ5}),-1.0]])]});}
            var Q56;
            {var subQ0=sQuery(id+"F1.wireOp",EDGE,"E4.3.5.0");var subQ5=sQuery(id+"F1.wireOp",EDGE,"E7.4.0.0");var subQ6=makeQuery(id+"F1.imprint","INTERSECT",VERTEX,{"derivedFrom":[subQ0,subQ5]});Q56=makeQuery(id+"F1.imprint","IMPRINT",FACE,{"disambiguationData":[TD([[makeQuery(id+"F1.imprint","IMPRINT",EDGE,{"disambiguationData":[TD([[subQ6,-1.0]])],"derivedFrom":subQ5}),-1.0]])]});}
            var Q57;
            {var subQ0=sQuery(id+"F1.wireOp",EDGE,"E4.2.5.0");var subQ5=sQuery(id+"F1.wireOp",EDGE,"E7.5.0.0");var subQ6=makeQuery(id+"F1.imprint","INTERSECT",VERTEX,{"derivedFrom":[subQ0,subQ5]});Q57=makeQuery(id+"F1.imprint","IMPRINT",FACE,{"disambiguationData":[TD([[makeQuery(id+"F1.imprint","IMPRINT",EDGE,{"disambiguationData":[TD([[subQ6,-1.0]])],"derivedFrom":subQ5}),-1.0]])]});}
            var Q58;
            {var subQ0=sQuery(id+"F1.wireOp",EDGE,"E4.1.5.0");var subQ5=sQuery(id+"F1.wireOp",EDGE,"E7.6.0.0");var subQ6=makeQuery(id+"F1.imprint","INTERSECT",VERTEX,{"derivedFrom":[subQ0,subQ5]});Q58=makeQuery(id+"F1.imprint","IMPRINT",FACE,{"disambiguationData":[TD([[makeQuery(id+"F1.imprint","IMPRINT",EDGE,{"disambiguationData":[TD([[subQ6,-1.0]])],"derivedFrom":subQ5}),-1.0]])]});}
            var Q59;
            {var subQ0=sQuery(id+"F1.wireOp",EDGE,"E6.0");var subQ1=sQuery(id+"F1.wireOp",EDGE,"E4.0.5.0");var subQ2=makeQuery(id+"F1.imprint","INTERSECT",VERTEX,{"derivedFrom":[subQ1,subQ0]});Q59=makeQuery(id+"F1.imprint","IMPRINT",FACE,{"disambiguationData":[TD([[makeQuery(id+"F1.imprint","IMPRINT",EDGE,{"disambiguationData":[TD([[subQ2,-1.0]])],"derivedFrom":subQ1}),-1.0]])]});}
            var Q60;
            {var subQ0=sQuery(id+"F1.wireOp",EDGE,"E4.5.6.0");var subQ5=sQuery(id+"F1.wireOp",EDGE,"E7.2.0.0");var subQ6=makeQuery(id+"F1.imprint","INTERSECT",VERTEX,{"derivedFrom":[subQ0,subQ5]});Q60=makeQuery(id+"F1.imprint","IMPRINT",FACE,{"disambiguationData":[TD([[makeQuery(id+"F1.imprint","IMPRINT",EDGE,{"disambiguationData":[TD([[subQ6,-1.0]])],"derivedFrom":subQ5}),-1.0]])]});}
            var Q61;
            {var subQ0=sQuery(id+"F1.wireOp",EDGE,"E4.4.6.0");var subQ5=sQuery(id+"F1.wireOp",EDGE,"E7.3.0.0");var subQ6=makeQuery(id+"F1.imprint","INTERSECT",VERTEX,{"derivedFrom":[subQ0,subQ5]});Q61=makeQuery(id+"F1.imprint","IMPRINT",FACE,{"disambiguationData":[TD([[makeQuery(id+"F1.imprint","IMPRINT",EDGE,{"disambiguationData":[TD([[subQ6,-1.0]])],"derivedFrom":subQ5}),-1.0]])]});}
            var Q62;
            {var subQ0=sQuery(id+"F1.wireOp",EDGE,"E4.3.6.0");var subQ5=sQuery(id+"F1.wireOp",EDGE,"E7.4.0.0");var subQ6=makeQuery(id+"F1.imprint","INTERSECT",VERTEX,{"derivedFrom":[subQ0,subQ5]});Q62=makeQuery(id+"F1.imprint","IMPRINT",FACE,{"disambiguationData":[TD([[makeQuery(id+"F1.imprint","IMPRINT",EDGE,{"disambiguationData":[TD([[subQ6,-1.0]])],"derivedFrom":subQ5}),-1.0]])]});}
            var Q63;
            {var subQ0=sQuery(id+"F1.wireOp",EDGE,"E4.2.6.0");var subQ5=sQuery(id+"F1.wireOp",EDGE,"E7.5.0.0");var subQ6=makeQuery(id+"F1.imprint","INTERSECT",VERTEX,{"derivedFrom":[subQ0,subQ5]});Q63=makeQuery(id+"F1.imprint","IMPRINT",FACE,{"disambiguationData":[TD([[makeQuery(id+"F1.imprint","IMPRINT",EDGE,{"disambiguationData":[TD([[subQ6,-1.0]])],"derivedFrom":subQ5}),-1.0]])]});}
            var Q64;
            {var subQ0=sQuery(id+"F1.wireOp",EDGE,"E4.1.6.0");var subQ5=sQuery(id+"F1.wireOp",EDGE,"E7.6.0.0");var subQ6=makeQuery(id+"F1.imprint","INTERSECT",VERTEX,{"derivedFrom":[subQ0,subQ5]});Q64=makeQuery(id+"F1.imprint","IMPRINT",FACE,{"disambiguationData":[TD([[makeQuery(id+"F1.imprint","IMPRINT",EDGE,{"disambiguationData":[TD([[subQ6,-1.0]])],"derivedFrom":subQ5}),-1.0]])]});}
            var Q65;
            {var subQ0=sQuery(id+"F1.wireOp",EDGE,"E6.0");var subQ1=sQuery(id+"F1.wireOp",EDGE,"E4.0.6.0");var subQ2=makeQuery(id+"F1.imprint","INTERSECT",VERTEX,{"derivedFrom":[subQ1,subQ0]});Q65=makeQuery(id+"F1.imprint","IMPRINT",FACE,{"disambiguationData":[TD([[makeQuery(id+"F1.imprint","IMPRINT",EDGE,{"disambiguationData":[TD([[subQ2,-1.0]])],"derivedFrom":subQ1}),-1.0]])]});}
            var Q66;
            {var subQ0=sQuery(id+"F1.wireOp",EDGE,"E6.0");var subQ1=sQuery(id+"F1.wireOp",EDGE,"E4.0.7.0");var subQ2=makeQuery(id+"F1.imprint","INTERSECT",VERTEX,{"derivedFrom":[subQ1,subQ0]});Q66=makeQuery(id+"F1.imprint","IMPRINT",FACE,{"disambiguationData":[TD([[makeQuery(id+"F1.imprint","IMPRINT",EDGE,{"disambiguationData":[TD([[subQ2,-1.0]])],"derivedFrom":subQ1}),-1.0]])]});}
            var Q67;
            {var subQ0=sQuery(id+"F1.wireOp",EDGE,"E4.1.7.0");var subQ5=sQuery(id+"F1.wireOp",EDGE,"E7.6.0.0");var subQ6=makeQuery(id+"F1.imprint","INTERSECT",VERTEX,{"derivedFrom":[subQ0,subQ5]});Q67=makeQuery(id+"F1.imprint","IMPRINT",FACE,{"disambiguationData":[TD([[makeQuery(id+"F1.imprint","IMPRINT",EDGE,{"disambiguationData":[TD([[subQ6,-1.0]])],"derivedFrom":subQ5}),-1.0]])]});}
            var Q68;
            {var subQ0=sQuery(id+"F1.wireOp",EDGE,"E4.2.7.0");var subQ5=sQuery(id+"F1.wireOp",EDGE,"E7.5.0.0");var subQ6=makeQuery(id+"F1.imprint","INTERSECT",VERTEX,{"derivedFrom":[subQ0,subQ5]});Q68=makeQuery(id+"F1.imprint","IMPRINT",FACE,{"disambiguationData":[TD([[makeQuery(id+"F1.imprint","IMPRINT",EDGE,{"disambiguationData":[TD([[subQ6,-1.0]])],"derivedFrom":subQ5}),-1.0]])]});}
            var Q69;
            {var subQ0=sQuery(id+"F1.wireOp",EDGE,"E4.3.7.0");var subQ5=sQuery(id+"F1.wireOp",EDGE,"E7.4.0.0");var subQ6=makeQuery(id+"F1.imprint","INTERSECT",VERTEX,{"derivedFrom":[subQ0,subQ5]});Q69=makeQuery(id+"F1.imprint","IMPRINT",FACE,{"disambiguationData":[TD([[makeQuery(id+"F1.imprint","IMPRINT",EDGE,{"disambiguationData":[TD([[subQ6,-1.0]])],"derivedFrom":subQ5}),-1.0]])]});}
            var Q70;
            {var subQ0=sQuery(id+"F1.wireOp",EDGE,"E4.4.7.0");var subQ5=sQuery(id+"F1.wireOp",EDGE,"E7.3.0.0");var subQ6=makeQuery(id+"F1.imprint","INTERSECT",VERTEX,{"derivedFrom":[subQ0,subQ5]});Q70=makeQuery(id+"F1.imprint","IMPRINT",FACE,{"disambiguationData":[TD([[makeQuery(id+"F1.imprint","IMPRINT",EDGE,{"disambiguationData":[TD([[subQ6,-1.0]])],"derivedFrom":subQ5}),-1.0]])]});}
            var Q71;
            {var subQ0=sQuery(id+"F1.wireOp",EDGE,"E4.5.7.0");var subQ5=sQuery(id+"F1.wireOp",EDGE,"E7.2.0.0");var subQ6=makeQuery(id+"F1.imprint","INTERSECT",VERTEX,{"derivedFrom":[subQ0,subQ5]});Q71=makeQuery(id+"F1.imprint","IMPRINT",FACE,{"disambiguationData":[TD([[makeQuery(id+"F1.imprint","IMPRINT",EDGE,{"disambiguationData":[TD([[subQ6,-1.0]])],"derivedFrom":subQ5}),-1.0]])]});}
            extrude(context, id + "F3", {"entities" : qUnion([Q0, Q1, Q2, Q3, Q4, Q5, Q6, Q7, Q8, Q9, Q10, Q11, Q12, Q13, Q14, Q15, Q16, Q17, Q18, Q19, Q20, Q21, Q22, Q23, Q24, Q25, Q26, Q27, Q28, Q29, Q30, Q31, Q32, Q33, Q34, Q35, Q36, Q37, Q38, Q39, Q40, Q41, Q42, Q43, Q44, Q45, Q46, Q47, Q48, Q49, Q50, Q51, Q52, Q53, Q54, Q55, Q56, Q57, Q58, Q59, Q60, Q61, Q62, Q63, Q64, Q65, Q66, Q67, Q68, Q69, Q70, Q71]), "operationType" : NewBodyOperationType.ADD, "depth" : 16.76 * mm});
        }
        {
            var Q0;
            Q0=makeQuery(id+"F1.imprint","IMPRINT",FACE,{"disambiguationData":[TD([[makeQuery(id+"F1.imprint","IMPRINT",EDGE,{"derivedFrom":sQuery(id+"F1.wireOp",EDGE,"E1.right")}),1.0]])]});
            extrude(context, id + "F4", {"entities" : qUnion([Q0]), "operationType" : NewBodyOperationType.ADD, "depth" : 17.02 * mm});
        }
    });
